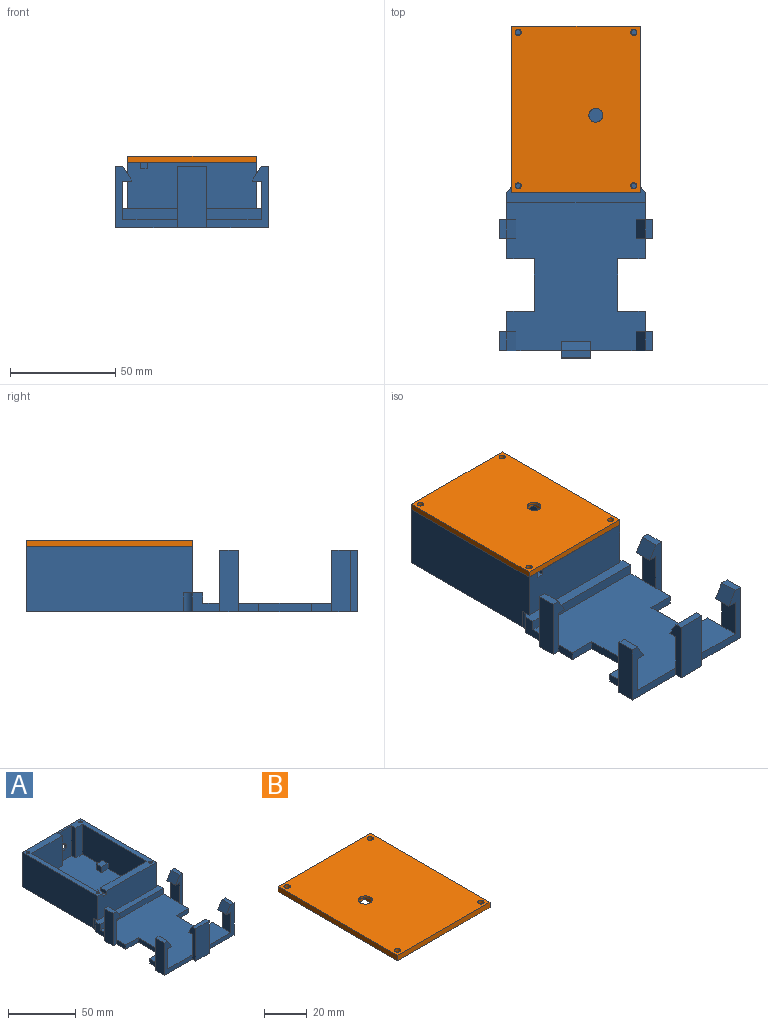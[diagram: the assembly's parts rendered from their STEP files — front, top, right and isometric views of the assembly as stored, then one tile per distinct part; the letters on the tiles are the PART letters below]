
ASSEMBLY  parts=2 mates=1
PART A: 90 faces, bbox 72.7x157.8x31 mm
  f0: plane 18.2x9mm, normal (1,0,0), area 163.8mm2, adj f3,f10,f12,f81
  f1: plane 18.2x9mm, normal (-1,0,0), area 163.8mm2, adj f3,f32,f34,f80
  f2: plane 18.2x14mm, normal (0,1,0), area 254.8mm2, adj f3,f21,f23,f73
  f3: plane 70.3x65.7mm, normal (0,0,1), area 3968.7mm2, adj f0,f1,f2,f9,f13,f14,f15,f16
  f4: plane 67x27mm, normal (-1,0,0), area 1752.5mm2, adj f5,f39,f42,f44,f47,f55,f60,f62
  f5: plane 66x53mm, normal (0,0,1), area 3060.3mm2, adj f4,f39,f40,f41,f43,f45,f46,f47
  f6: plane 79x31mm, normal (1,0,0), area 2410.8mm2, adj f7,f38,f54,f55,f72,f84
  f7: plane 61x31mm, normal (0,1,0), area 1796.7mm2, adj f6,f8,f38,f55,f85,f86
  f8: plane 79x31mm, normal (-1,0,0), area 2410.8mm2, adj f7,f38,f54,f55,f72,f83
  f9: plane 13x9mm, normal (-1,0,0), area 77mm2, adj f3,f10,f38,f71,f72,f83
  f10: plane 29.2x7.8mm, normal (0,1,0), area 117.3mm2, adj f0,f9,f11,f38,f65,f81,f82
  f11: plane 29.2x9mm, normal (-1,0,0), area 262.8mm2, adj f10,f12,f38,f65
  f12: plane 29.2x7.8mm, normal (0,-1,0), area 117.3mm2, adj f0,f11,f13,f38,f65,f81,f82
  f13: plane 9.65x4mm, normal (-1,0,0), area 38.6mm2, adj f3,f12,f14,f38
  f14: plane 13x4mm, normal (0,-1,0), area 52mm2, adj f3,f13,f15,f38
  f15: plane 25x4mm, normal (-1,0,0), area 100mm2, adj f3,f14,f16,f38
  f16: plane 13x4mm, normal (0,1,0), area 52mm2, adj f3,f15,f17,f38
  f17: plane 9.65x4mm, normal (-1,0,0), area 38.6mm2, adj f3,f16,f18,f38
  f18: plane 29.2x7.8mm, normal (0,1,0), area 117.3mm2, adj f17,f19,f38,f66,f67,f77,f78
  f19: plane 29.2x9mm, normal (-1,0,0), area 262.8mm2, adj f18,f20,f38,f67
  f20: plane 29.35x29.2mm, normal (0,-1,0), area 220.7mm2, adj f3,f19,f21,f38,f66,f67,f77,f78
  f21: plane 29.2x7.8mm, normal (-1,0,0), area 117.3mm2, adj f2,f20,f22,f38,f70,f73,f74
  f22: plane 29.2x14mm, normal (0,-1,0), area 408.8mm2, adj f21,f23,f38,f70
  f23: plane 29.2x7.8mm, normal (1,0,0), area 117.3mm2, adj f2,f22,f24,f38,f70,f73,f74
  f24: plane 29.35x29.2mm, normal (0,-1,0), area 220.7mm2, adj f3,f23,f25,f38,f68,f69,f75,f76
  f25: plane 29.2x9mm, normal (1,0,0), area 262.8mm2, adj f24,f26,f38,f69
  f26: plane 29.2x7.8mm, normal (0,1,0), area 117.3mm2, adj f25,f27,f38,f68,f69,f75,f76
  f27: plane 9.65x4mm, normal (1,0,0), area 38.6mm2, adj f3,f26,f28,f38
  f28: plane 13x4mm, normal (0,1,0), area 52mm2, adj f3,f27,f29,f38
  f29: plane 25x4mm, normal (1,0,0), area 100mm2, adj f3,f28,f30,f38
  f30: plane 13x4mm, normal (0,-1,0), area 52mm2, adj f3,f29,f31,f38
  f31: plane 9.65x4mm, normal (1,0,0), area 38.6mm2, adj f3,f30,f32,f38
  f32: plane 29.2x7.8mm, normal (0,-1,0), area 117.2mm2, adj f1,f31,f33,f38,f64,f79,f80
  f33: plane 29.2x9mm, normal (1,0,0), area 262.8mm2, adj f32,f34,f38,f64
  f34: plane 29.2x7.8mm, normal (0,1,0), area 117.2mm2, adj f1,f33,f35,f38,f64,f79,f80
  f35: plane 13x9mm, normal (1,0,0), area 77mm2, adj f3,f34,f38,f71,f72,f84
  f36: cylinder r=1.28mm len=9mm, axis (0,0,1), area 72.1mm2, adj f38,f42
  f37: cylinder r=1.28mm len=9mm, axis (0,0,1), area 72.1mm2, adj f38,f42
  f38: plane 157.8x72.7mm, normal (0,0,-1), area 9286.9mm2, adj f6,f7,f8,f9,f10,f11,f12,f13
  f39: plane 47.5x5mm, normal (0,1,0), area 237.5mm2, adj f4,f5,f40,f42
  f40: plane 40.5x5mm, normal (1,0,0), area 202.5mm2, adj f5,f39,f41,f42
  f41: plane 5.5x5mm, normal (0,1,0), area 27.5mm2, adj f5,f40,f42,f43
  f42: plane 53x46mm, normal (0,0,1), area 504mm2, adj f4,f36,f37,f39,f40,f41,f43,f44
  f43: plane 67x27mm, normal (1,0,0), area 1579mm2, adj f5,f41,f42,f44,f48,f55
  f44: plane 53x22mm, normal (0,1,0), area 1156.4mm2, adj f4,f42,f43,f55,f87,f88,f89
  f45: plane 27x14mm, normal (0,-1,0), area 348.8mm2, adj f5,f46,f53,f55,f86
  f46: plane 27x4.5mm, normal (-1,0,0), area 121.5mm2, adj f5,f45,f47,f55
  f47: plane 27x7mm, normal (0,-1,0), area 189mm2, adj f4,f5,f46,f55
  f48: plane 32x27mm, normal (0,-1,0), area 799mm2, adj f5,f43,f53,f55,f85
  f49: cylinder r=1.28mm len=27mm, axis (0,0,-1), area 216.3mm2, adj f55,f56
  f50: cylinder r=1.28mm len=27mm, axis (0,0,-1), area 216.3mm2, adj f55,f57
  f51: cylinder r=1.28mm len=27mm, axis (0,0,-1), area 216.3mm2, adj f55,f58
  f52: cylinder r=1.28mm len=27mm, axis (0,0,-1), area 216.3mm2, adj f55,f59
  f53: plane 27x4.5mm, normal (1,0,0), area 121.5mm2, adj f5,f45,f48,f55
  f54: plane 61x22mm, normal (0,-1,0), area 1332.4mm2, adj f6,f8,f55,f72,f87,f88,f89
  f55: plane 79x61mm, normal (0,0,1), area 1165.4mm2, adj f4,f6,f7,f8,f43,f44,f45,f46
  f56: plane 2.55x2.55mm, normal (0,0,1), area 5.1mm2, adj f49
  f57: plane 2.55x2.55mm, normal (0,0,1), area 5.1mm2, adj f50
  f58: plane 2.55x2.55mm, normal (0,0,1), area 5.1mm2, adj f51
  f59: plane 2.55x2.55mm, normal (0,0,1), area 5.1mm2, adj f52
  f60: plane 6.8x5mm, normal (0,1,0), area 34mm2, adj f4,f5,f61,f63
  f61: plane 5.8x5mm, normal (-1,0,0), area 29mm2, adj f5,f60,f62,f63
  f62: plane 6.8x5mm, normal (0,-1,0), area 34mm2, adj f4,f5,f61,f63
  f63: plane 6.8x5.8mm, normal (0,0,1), area 39.4mm2, adj f4,f60,f61,f62
  f64: plane 9x3.5mm, normal (0,0,1), area 31.5mm2, adj f32,f33,f34,f79
  f65: plane 9x3.5mm, normal (0,0,1), area 31.5mm2, adj f10,f11,f12,f82
  f66: plane 18.2x9mm, normal (1,0,0), area 163.8mm2, adj f3,f18,f20,f77
  f67: plane 9x3.5mm, normal (0,0,1), area 31.5mm2, adj f18,f19,f20,f78
  f68: plane 18.2x9mm, normal (-1,0,0), area 163.8mm2, adj f3,f24,f26,f76
  f69: plane 9x3.5mm, normal (0,0,1), area 31.5mm2, adj f24,f25,f26,f75
  f70: plane 14x3.5mm, normal (0,0,1), area 49mm2, adj f21,f22,f23,f74
  f71: plane 65.7x5mm, normal (0,-1,0), area 328.5mm2, adj f3,f9,f35,f72
  f72: plane 65.7x9.24mm, normal (0,0,1), area 334.4mm2, adj f6,f8,f9,f35,f54,f71,f83,f84
  f73: plane 14x4.3mm, normal (0,0,-1), area 60.2mm2, adj f2,f21,f23,f74
  f74: plane 14x7mm, normal (0,0.85,0.52), area 115mm2, adj f21,f23,f70,f73
  f75: plane 9x7mm, normal (-0.85,0,0.52), area 73.9mm2, adj f24,f26,f69,f76
  f76: plane 9x4.3mm, normal (0,0,-1), area 38.7mm2, adj f24,f26,f68,f75
  f77: plane 9x4.3mm, normal (0,0,-1), area 38.7mm2, adj f18,f20,f66,f78
  f78: plane 9x7mm, normal (0.85,0,0.52), area 73.9mm2, adj f18,f20,f67,f77
  f79: plane 9x7mm, normal (-0.85,0,0.52), area 73.9mm2, adj f32,f34,f64,f80
  f80: plane 9x4.3mm, normal (0,0,-1), area 38.7mm2, adj f1,f32,f34,f79
  f81: plane 9x4.3mm, normal (0,0,-1), area 38.7mm2, adj f0,f10,f12,f82
  f82: plane 9x7mm, normal (0.85,0,0.52), area 73.9mm2, adj f10,f12,f65,f81
  f83: cylinder r=5mm len=9mm, axis (0,0,-1), area 45.5mm2, adj f8,f9,f38,f72
  f84: cylinder r=5mm len=9mm, axis (0,0,-1), area 45.5mm2, adj f6,f35,f38,f72
  f85: cylinder r=4.55mm len=9.1mm, axis (0,1,0), area 171.5mm2, adj f7,f48
  f86: cylinder r=3.05mm len=6.1mm, axis (0,1,0), area 28.7mm2, adj f7,f45
  f87: plane 6x3mm, normal (-1,0,0), area 18mm2, adj f44,f54,f55,f89
  f88: plane 6x3mm, normal (1,0,0), area 18mm2, adj f44,f54,f55,f89
  f89: plane 6x3.2mm, normal (0,0,1), area 19.2mm2, adj f44,f54,f87,f88
PART B: 21 faces, bbox 61x79x4.9 mm
  f0: plane 79x61mm, normal (0,0,-1), area 4550.9mm2, adj f1,f2,f3,f4,f5,f6,f7,f8
  f1: plane 79x3mm, normal (-1,0,0), area 237mm2, adj f0,f2,f4,f10
  f2: plane 61x3mm, normal (0,-1,0), area 183mm2, adj f0,f1,f3,f10
  f3: plane 79x3mm, normal (1,0,0), area 237mm2, adj f0,f2,f4,f10
  f4: plane 61x3mm, normal (0,1,0), area 183mm2, adj f0,f1,f3,f10
  f5: cylinder r=1.45mm len=3mm, axis (0,0,-1), area 27.3mm2, adj f0,f10
  f6: cylinder r=1.45mm len=3mm, axis (0,0,-1), area 27.3mm2, adj f0,f10
  f7: cylinder r=1.45mm len=3mm, axis (0,0,-1), area 27.3mm2, adj f0,f10
  f8: cylinder r=1.45mm len=3mm, axis (0,0,-1), area 27.3mm2, adj f0,f10
  f9: cylinder r=3.3mm len=6.6mm, axis (0,0,-1), area 22.8mm2, adj f10,f15
  f10: plane 79x61mm, normal (0,0,1), area 4758.4mm2, adj f1,f2,f3,f4,f5,f6,f7,f8
  f11: plane 10.9x3.8mm, normal (-1,0,0), area 41.4mm2, adj f12,f14,f15,f20
  f12: plane 10.2x3.8mm, normal (0,-1,0), area 38.8mm2, adj f11,f13,f15,f20
  f13: plane 10.9x3.8mm, normal (1,0,0), area 41.4mm2, adj f12,f14,f15,f20
  f14: plane 10.2x3.8mm, normal (0,1,0), area 38.8mm2, adj f11,f13,f15,f20
  f15: plane 10.9x10.2mm, normal (0,0,-1), area 77mm2, adj f9,f11,f12,f13,f14
  f16: plane 15.9x1.9mm, normal (1,0,0), area 30.2mm2, adj f0,f17,f19,f20
  f17: plane 15.2x1.9mm, normal (0,1,0), area 28.9mm2, adj f0,f16,f18,f20
  f18: plane 15.9x1.9mm, normal (-1,0,0), area 30.2mm2, adj f0,f17,f19,f20
  f19: plane 15.2x1.9mm, normal (0,-1,0), area 28.9mm2, adj f0,f16,f18,f20
  f20: plane 15.9x15.2mm, normal (0,0,-1), area 130.5mm2, adj f11,f12,f13,f14,f16,f17,f18,f19
PLACE A t=(0.03,29.31,-11.67)mm
PLACE B rot(axis=(0,0,1),180deg) t=(0.03,39.31,15.33)mm
MATE fastened B.f0 <-> A.f55  axis (0,0,-1) through (30.53,78.81,15.33)mm
